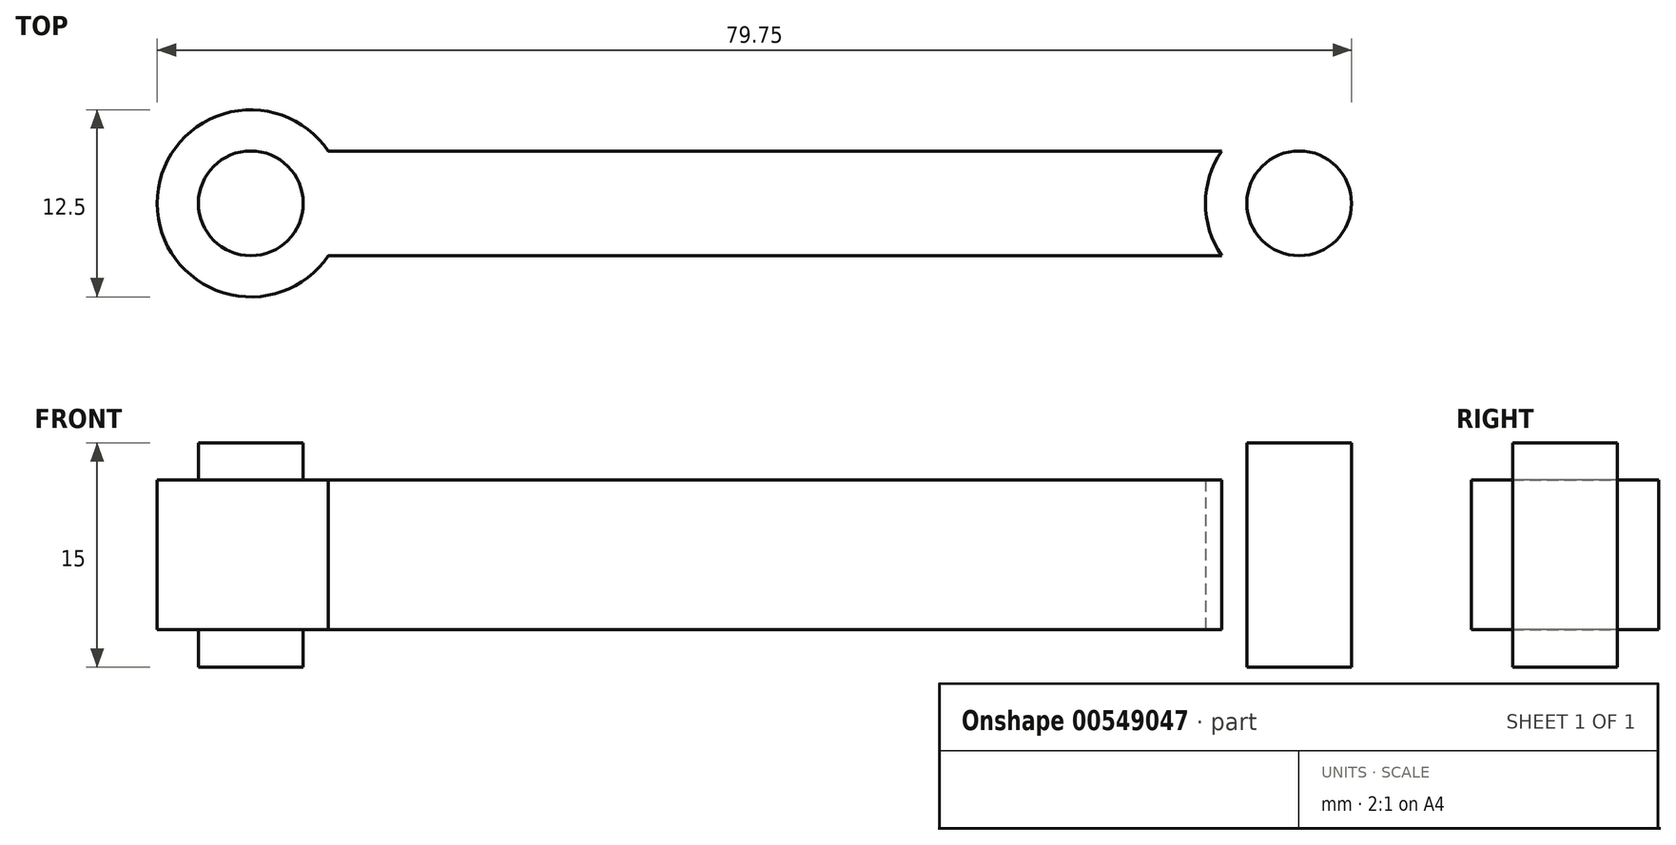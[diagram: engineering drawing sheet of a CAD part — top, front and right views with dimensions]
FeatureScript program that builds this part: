
annotation { "Feature Type Name" : "Feature", "Feature Type Description" : "" }
export const myFeature = defineFeature(function(context is Context, id is Id, definition is map)
    precondition{}
    {
        {
            var Q0;
            Q0=qCreatedBy(makeId("Top.planeOp"),FACE);
            var sketch = newSketch(context, id + "F0", { "sketchPlane" : qUnion([Q0])});
            skLineSegment(sketch, "E0.bottom", {"start": v(0, 0) * mm, "end": v(-35, 0) * mm});
            skLineSegment(sketch, "E0.top", {"start": v(0, 7) * mm, "end": v(-35, 7) * mm});
            skLineSegment(sketch, "E0.right", {"start": v(-35, 0) * mm, "end": v(-35, 7) * mm});
            skCircle(sketch, "E1", {"center": v(-35, 3.5) * mm, "radius": 6.25 * mm});
            skCircle(sketch, "E2", {"center": v(-35, 3.5) * mm, "radius": 3.5 * mm});
            skLineSegment(sketch, "E3", {"start": v(0, 51.48) * mm, "end": v(0, -30.03) * mm, "construction": true});
            skLineSegment(sketch, "E4.MirrorCS", {"start": v(35, 0) * mm, "end": v(35, 7) * mm});
            skLineSegment(sketch, "E5.MirrorCS", {"start": v(0, 0) * mm, "end": v(35, 0) * mm});
            skLineSegment(sketch, "E6.MirrorCS", {"start": v(0, 7) * mm, "end": v(35, 7) * mm});
            skCircle(sketch, "E7.MirrorC", {"center": v(35, 3.5) * mm, "radius": 6.25 * mm});
            skCircle(sketch, "E8.MirrorC", {"center": v(35, 3.5) * mm, "radius": 3.5 * mm});
            skSolve(sketch);
        }
        {
            var Q0;
            {var subQ1=sQuery(id+"F0.wireOp",EDGE,"E0.bottom");var subQ7=sQuery(id+"F0.wireOp",EDGE,"E5.MirrorCS");var subQ8=makeQuery(id+"F0.imprint","INTERSECT",VERTEX,{"derivedFrom":[subQ1,subQ7]});Q0=makeQuery(id+"F0.imprint","IMPRINT",FACE,{"disambiguationData":[TD([[makeQuery(id+"F0.imprint","IMPRINT",EDGE,{"disambiguationData":[TD([[subQ8,-1.0]])],"derivedFrom":subQ1}),-1.0]])]});}
            var Q1;
            {var subQ1=sQuery(id+"F0.wireOp",EDGE,"E5.MirrorCS");var subQ4=sQuery(id+"F0.wireOp",EDGE,"E7.MirrorC");var subQ5=makeQuery(id+"F0.imprint","INTERSECT",VERTEX,{"derivedFrom":[subQ1,subQ4]});Q1=makeQuery(id+"F0.imprint","IMPRINT",FACE,{"disambiguationData":[TD([[makeQuery(id+"F0.imprint","IMPRINT",EDGE,{"disambiguationData":[TD([[subQ5,-1.0]])],"derivedFrom":subQ4}),-1.0]])]});}
            var Q2;
            {var subQ1=sQuery(id+"F0.wireOp",EDGE,"E5.MirrorCS");var subQ4=sQuery(id+"F0.wireOp",EDGE,"E7.MirrorC");var subQ5=makeQuery(id+"F0.imprint","INTERSECT",VERTEX,{"derivedFrom":[subQ1,subQ4]});Q2=makeQuery(id+"F0.imprint","IMPRINT",FACE,{"disambiguationData":[TD([[makeQuery(id+"F0.imprint","IMPRINT",EDGE,{"disambiguationData":[TD([[subQ5,1.0]])],"derivedFrom":subQ4}),-1.0]])]});}
            var Q3;
            {var subQ2=sQuery(id+"F0.wireOp",EDGE,"E0.bottom");var subQ4=sQuery(id+"F0.wireOp",EDGE,"E1");var subQ5=makeQuery(id+"F0.imprint","INTERSECT",VERTEX,{"derivedFrom":[subQ2,subQ4]});Q3=makeQuery(id+"F0.imprint","IMPRINT",FACE,{"disambiguationData":[TD([[makeQuery(id+"F0.imprint","IMPRINT",EDGE,{"disambiguationData":[TD([[subQ5,-1.0]])],"derivedFrom":subQ4}),1.0]])]});}
            var Q4;
            {var subQ2=sQuery(id+"F0.wireOp",EDGE,"E0.bottom");var subQ4=sQuery(id+"F0.wireOp",EDGE,"E1");var subQ5=makeQuery(id+"F0.imprint","INTERSECT",VERTEX,{"derivedFrom":[subQ2,subQ4]});Q4=makeQuery(id+"F0.imprint","IMPRINT",FACE,{"disambiguationData":[TD([[makeQuery(id+"F0.imprint","IMPRINT",EDGE,{"disambiguationData":[TD([[subQ5,1.0]])],"derivedFrom":subQ4}),1.0]])]});}
            extrude(context, id + "F1", {"entities" : qUnion([Q0, Q1, Q2, Q3, Q4]), "endBound" : BoundingType.SYMMETRIC, "depth" : 10 * mm, "offsetDistance" : 25 * mm});
        }
        {
            var Q0;
            {var subQ0=sQuery(id+"F0.wireOp",EDGE,"E4.MirrorCS");Q0=makeQuery(id+"F0.imprint","IMPRINT",FACE,{"disambiguationData":[TD([[makeQuery(id+"F0.imprint","IMPRINT",EDGE,{"derivedFrom":subQ0}),1.0]])]});}
            var Q1;
            {var subQ0=sQuery(id+"F0.wireOp",EDGE,"E4.MirrorCS");Q1=makeQuery(id+"F0.imprint","IMPRINT",FACE,{"disambiguationData":[TD([[makeQuery(id+"F0.imprint","IMPRINT",EDGE,{"derivedFrom":subQ0}),-1.0]])]});}
            var Q2;
            {var subQ0=sQuery(id+"F0.wireOp",EDGE,"E0.right");Q2=makeQuery(id+"F0.imprint","IMPRINT",FACE,{"disambiguationData":[TD([[makeQuery(id+"F0.imprint","IMPRINT",EDGE,{"derivedFrom":subQ0}),1.0]])]});}
            var Q3;
            {var subQ0=sQuery(id+"F0.wireOp",EDGE,"E0.right");Q3=makeQuery(id+"F0.imprint","IMPRINT",FACE,{"disambiguationData":[TD([[makeQuery(id+"F0.imprint","IMPRINT",EDGE,{"derivedFrom":subQ0}),-1.0]])]});}
            extrude(context, id + "F2", {"entities" : qUnion([Q0, Q1, Q2, Q3]), "operationType" : NewBodyOperationType.ADD, "endBound" : BoundingType.SYMMETRIC, "depth" : 15 * mm, "offsetDistance" : 25 * mm});
        }
    });
